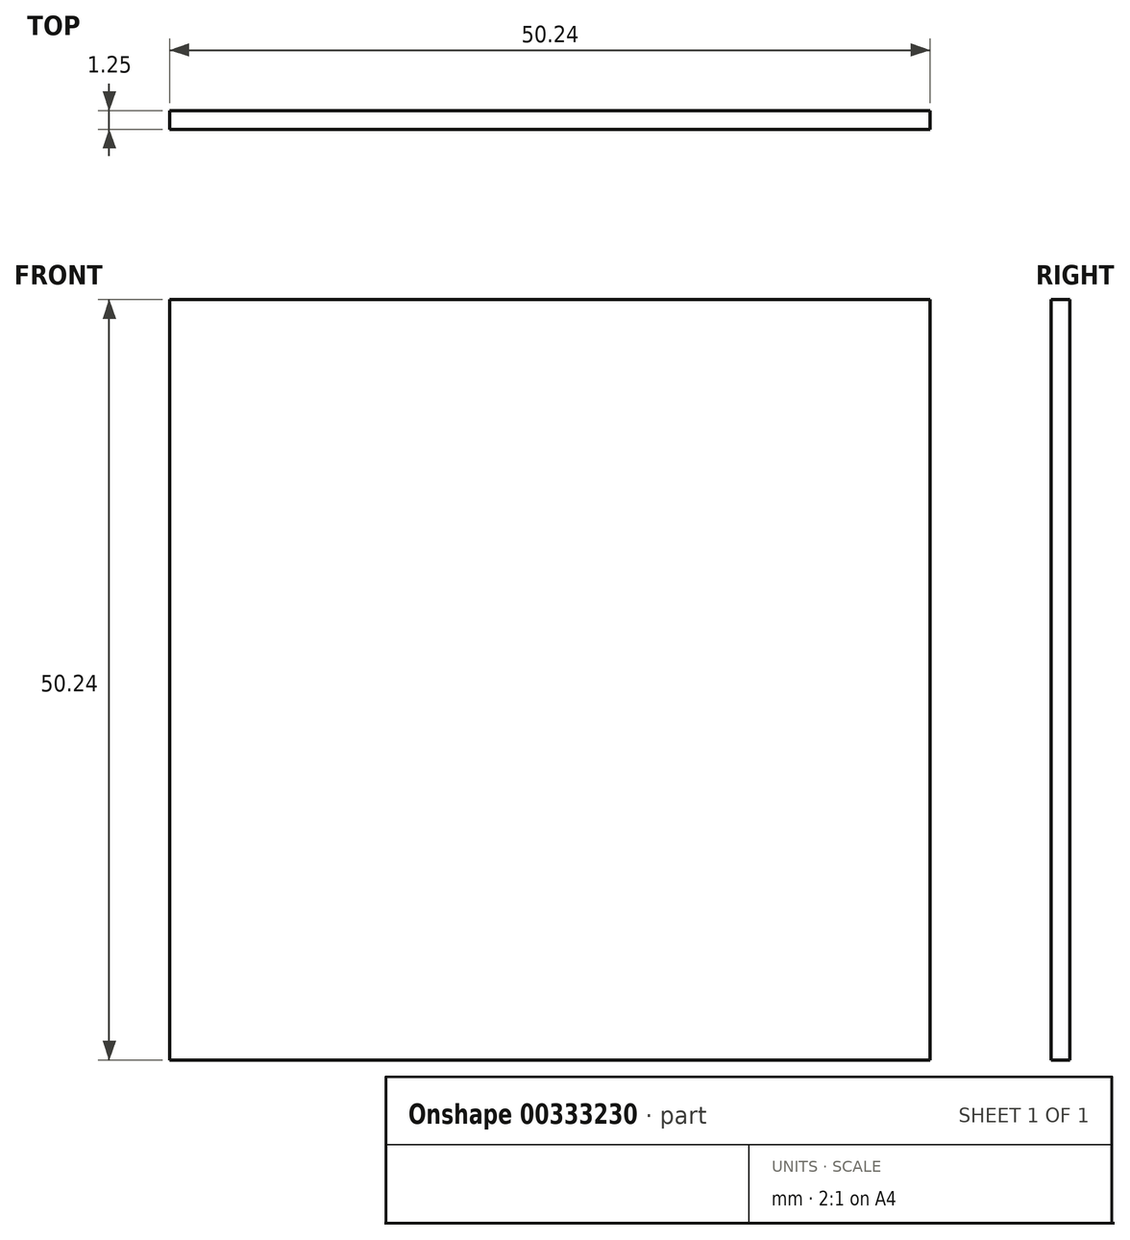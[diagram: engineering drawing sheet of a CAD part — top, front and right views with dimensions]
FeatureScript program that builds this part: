
annotation { "Feature Type Name" : "Feature", "Feature Type Description" : "" }
export const myFeature = defineFeature(function(context is Context, id is Id, definition is map)
    precondition{}
    {
        {
            var Q0;
            Q0=qCreatedBy(makeId("Front.planeOp"),FACE);
            var sketch = newSketch(context, id + "F0", { "sketchPlane" : qUnion([Q0])});
            skLineSegment(sketch, "E0.bottom", {"start": v(25.12, -25.12) * mm, "end": v(-25.12, -25.13) * mm});
            skLineSegment(sketch, "E0.top", {"start": v(25.12, 25.13) * mm, "end": v(-25.12, 25.12) * mm});
            skLineSegment(sketch, "E0.left", {"start": v(25.12, -25.12) * mm, "end": v(25.12, 25.13) * mm});
            skLineSegment(sketch, "E0.right", {"start": v(-25.12, -25.13) * mm, "end": v(-25.12, 25.12) * mm});
            skPoint(sketch, "E0.middle", {"position": v(0, 0) * mm});
            skSolve(sketch);
        }
        {
            var Q0;
            Q0=qSketchRegion(id+"F0",true);
            extrude(context, id + "F1", {"entities" : qUnion([Q0]), "depth" : 1.25 * mm});
        }
    });
